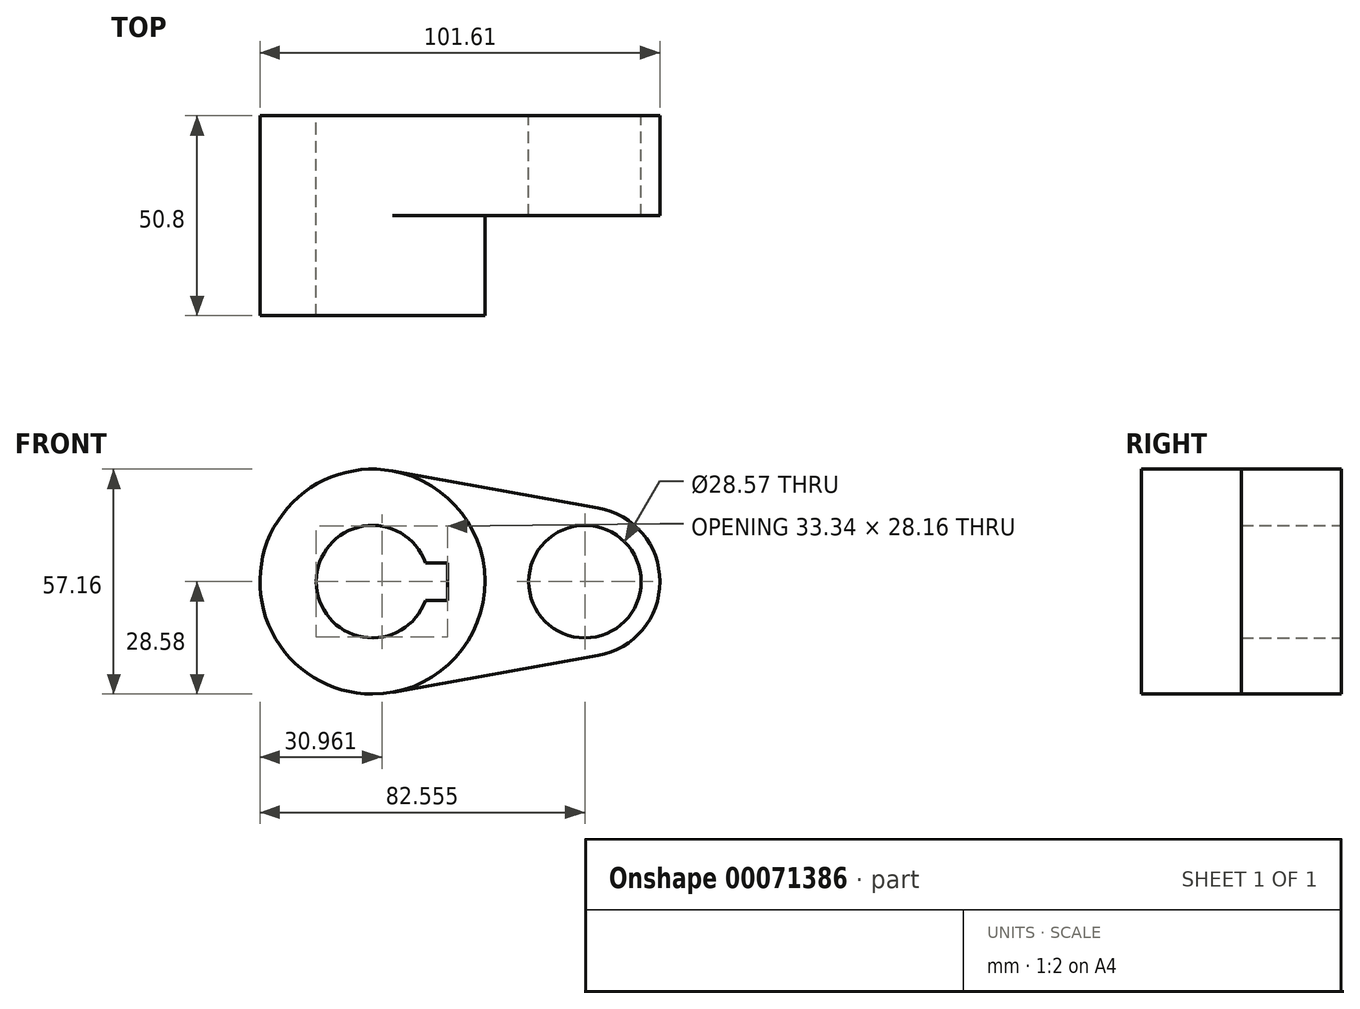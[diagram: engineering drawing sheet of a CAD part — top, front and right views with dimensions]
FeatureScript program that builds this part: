
annotation { "Feature Type Name" : "Feature", "Feature Type Description" : "" }
export const myFeature = defineFeature(function(context is Context, id is Id, definition is map)
    precondition{}
    {
        {
            var Q0;
            Q0=qCreatedBy(makeId("Front.planeOp"),FACE);
            var sketch = newSketch(context, id + "F0", { "sketchPlane" : qUnion([Q0])});
            skCircle(sketch, "E0", {"center": v(0, 0) * mm, "radius": 28.57 * mm});
            skCircle(sketch, "E1", {"center": v(53.98, 0) * mm, "radius": 19.05 * mm});
            skLineSegment(sketch, "E2", {"start": v(5.04, 28.13) * mm, "end": v(57.34, 18.75) * mm});
            skLineSegment(sketch, "E3", {"start": v(57.34, -18.75) * mm, "end": v(5.04, -28.13) * mm});
            skCircle(sketch, "E4", {"center": v(0, 0) * mm, "radius": 14.29 * mm});
            skCircle(sketch, "E5", {"center": v(53.98, 0) * mm, "radius": 14.29 * mm});
            skLineSegment(sketch, "E6.rect.bottom", {"start": v(19.05, -4.76) * mm, "end": v(-19.05, -4.76) * mm});
            skLineSegment(sketch, "E6.rect.top", {"start": v(19.05, 4.76) * mm, "end": v(-19.05, 4.76) * mm});
            skLineSegment(sketch, "E6.rect.left", {"start": v(19.05, -4.76) * mm, "end": v(19.05, 4.76) * mm});
            skLineSegment(sketch, "E6.rect.right", {"start": v(-19.05, -4.76) * mm, "end": v(-19.05, 4.76) * mm});
            skSolve(sketch);
        }
        {
            var Q0;
            {var subQ11=sQuery(id+"F0.wireOp",EDGE,"E6.rect.left");Q0=makeQuery(id+"F0.imprint","IMPRINT",FACE,{"disambiguationData":[TD([[makeQuery(id+"F0.imprint","IMPRINT",EDGE,{"derivedFrom":subQ11}),-1.0]])]});}
            var Q1;
            {var subQ0=sQuery(id+"F0.wireOp",EDGE,"E2");Q1=makeQuery(id+"F0.imprint","IMPRINT",FACE,{"disambiguationData":[TD([[makeQuery(id+"F0.imprint","IMPRINT",EDGE,{"derivedFrom":subQ0}),-1.0]])]});}
            var Q2;
            Q2=makeQuery(id+"F0.imprint","IMPRINT",FACE,{"disambiguationData":[TD([[makeQuery(id+"F0.imprint","IMPRINT",EDGE,{"derivedFrom":sQuery(id+"F0.wireOp",EDGE,"E5")}),-1.0]])]});
            var Q3;
            {var subQ5=sQuery(id+"F0.wireOp",EDGE,"E6.rect.right");Q3=makeQuery(id+"F0.imprint","IMPRINT",FACE,{"disambiguationData":[TD([[makeQuery(id+"F0.imprint","IMPRINT",EDGE,{"derivedFrom":subQ5}),-1.0]])]});}
            extrude(context, id + "F1", {"entities" : qUnion([Q0, Q1, Q2, Q3]), "depth" : 25.4 * mm});
        }
        {
            var Q0;
            {var subQ11=sQuery(id+"F0.wireOp",EDGE,"E6.rect.left");Q0=makeQuery(id+"F0.imprint","IMPRINT",FACE,{"disambiguationData":[TD([[makeQuery(id+"F0.imprint","IMPRINT",EDGE,{"derivedFrom":subQ11}),-1.0]])]});}
            var Q1;
            {var subQ5=sQuery(id+"F0.wireOp",EDGE,"E6.rect.right");Q1=makeQuery(id+"F0.imprint","IMPRINT",FACE,{"disambiguationData":[TD([[makeQuery(id+"F0.imprint","IMPRINT",EDGE,{"derivedFrom":subQ5}),-1.0]])]});}
            extrude(context, id + "F2", {"entities" : qUnion([Q0, Q1]), "operationType" : NewBodyOperationType.ADD, "depth" : 50.8 * mm});
        }
    });
